# Revit family: Lodestar 12' x 12' Family - Sharable - 11-24
name_source: partatom
category: Generic Models
units: mm (PartAtom-declared; Revit-internal decimal feet)

## family parameters
Always vertical = Yes
Can host rebar = No
Cut with Voids When Loaded = No
Maintain Annotation Orientation = No
Part Type = Normal
Room Calculation Point = No
Round Connector Dimension = Use Diameter
Shared = No
Work Plane-Based = No

## types (4) — shared parameters
Column Grout Y/N = No
Concrete Material = Concrete, LODESTAR Module
Corner Pillars_LxW = 350 mm
Fastener Material = <By Category>
Grout Material = <By Category>
Isolated Columns Y/N = Yes
LODESTAR Module_L = 9000 mm
LODESTAR Module_W = 4500 mm
Material Steel = Steel
Structural Connection = Yes
Structural Fasteners = Yes
Surface Bulkhead_D = 250 mm  [stored 0.82021 ft]
Utility Transfer Ports_H = 100 mm  [stored 0.328084 ft]
module_mainChamfer = 40 mm
steelFooting_connectionHeight = 125 mm
steelFooting_plateSquare = 270 mm
steelFooting_plateThickness = 13 mm
zero-valued in all types: Default Elevation

## per-type parameters (varying)
| type | Base Plate Y/N | Base visibility Y/N | Lifting Hooks Y/N | Lifting Material | Panel Connections (Female) Y/N | Poured Base Y/N | Steel Material | system_beamsTOP | system_centerBeamTOP | system_utilityPort-436 |
| Module + Base W/ Connections | Yes | Yes | Yes | Copper | Yes | Yes | Steel | Yes | Yes | Yes |
| Module | No | No | No | <By Category> | No | No | <By Category> | Yes | Yes | Yes |
| Module + Base | Yes | Yes | Yes | <By Category> | No | No | <By Category> | Yes | Yes | Yes |
| Isolated Column | No | No | No | <By Category> | No | No | <By Category> | No | No | No |

note: [stored X ft] marks values corroborated as IEEE doubles in the binary element streams (Revit-internal decimal feet)

## geometry (parser evidence)
native form markers: Sweep x6
no freeform markers — native parametric forms only
